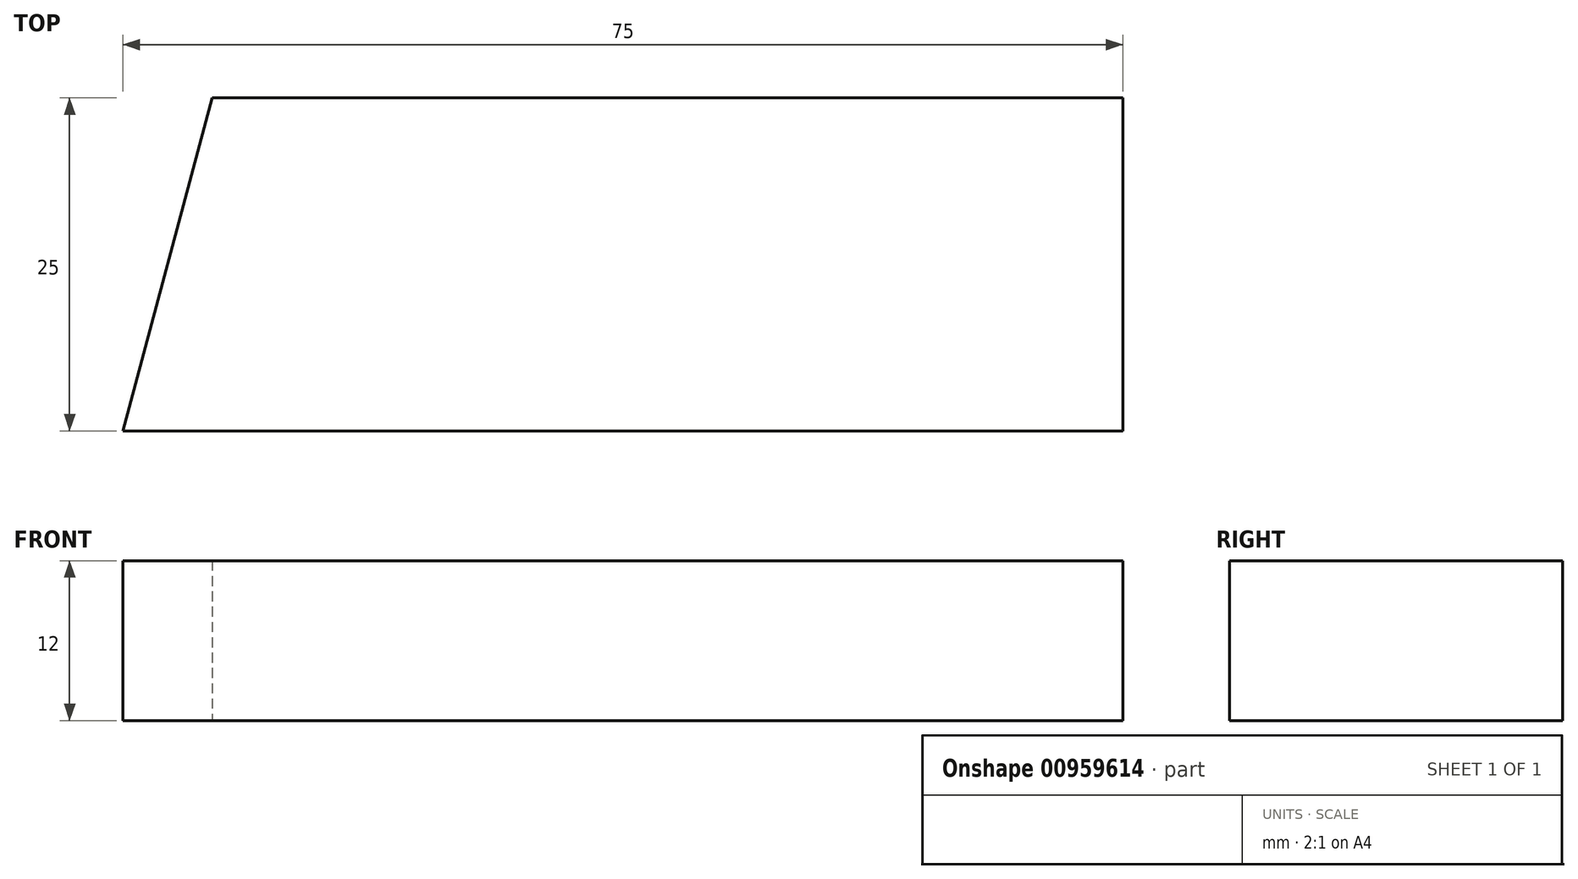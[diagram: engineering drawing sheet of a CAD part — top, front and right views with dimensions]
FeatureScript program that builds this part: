
annotation { "Feature Type Name" : "Feature", "Feature Type Description" : "" }
export const myFeature = defineFeature(function(context is Context, id is Id, definition is map)
    precondition{}
    {
        {
            var Q0;
            Q0=qCreatedBy(makeId("Top.planeOp"),FACE);
            var sketch = newSketch(context, id + "F0", { "sketchPlane" : qUnion([Q0])});
            skLineSegment(sketch, "E0", {"start": v(0, 0) * mm, "end": v(75, 0) * mm});
            skLineSegment(sketch, "E1", {"start": v(75, 0) * mm, "end": v(75, 25) * mm});
            skLineSegment(sketch, "E2", {"start": v(75, 25) * mm, "end": v(6.7, 25) * mm});
            skLineSegment(sketch, "E3", {"start": v(6.7, 25) * mm, "end": v(0, 0) * mm});
            skSolve(sketch);
        }
        {
            var Q0;
            Q0=makeQuery(id+"F0.imprint","IMPRINT",FACE,{"disambiguationData":[TD([[makeQuery(id+"F0.imprint","IMPRINT",EDGE,{"derivedFrom":sQuery(id+"F0.wireOp",EDGE,"E0")}),1.0]])]});
            extrude(context, id + "F1", {"entities" : qUnion([Q0]), "depth" : 12 * mm, "offsetDistance" : 25 * mm});
        }
    });
